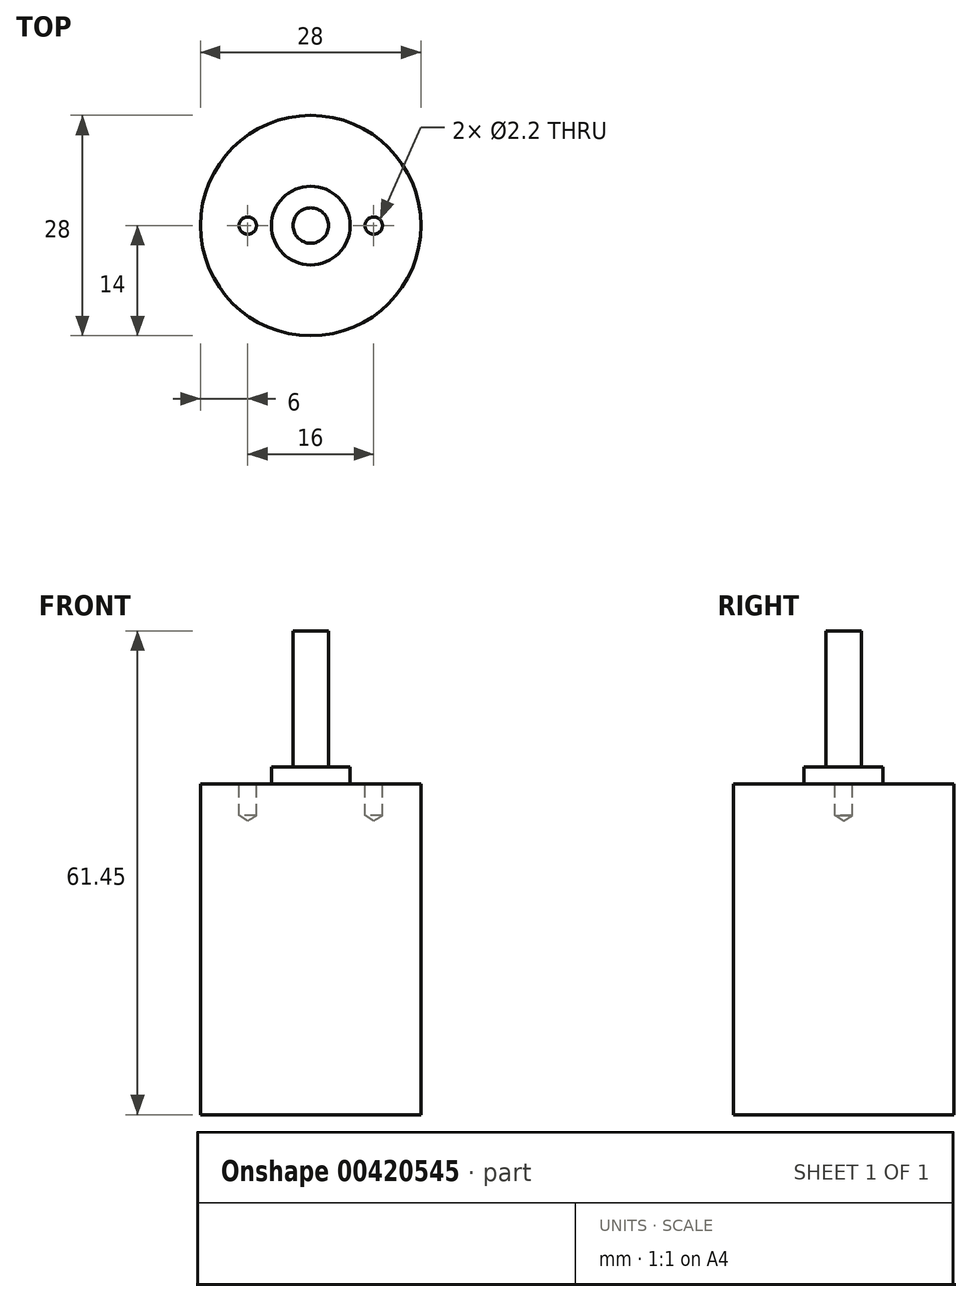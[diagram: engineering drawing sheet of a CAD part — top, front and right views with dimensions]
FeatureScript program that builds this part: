
annotation { "Feature Type Name" : "Feature", "Feature Type Description" : "" }
export const myFeature = defineFeature(function(context is Context, id is Id, definition is map)
    precondition{}
    {
        {
            var Q0;
            Q0=qCreatedBy(makeId("Top.planeOp"),FACE);
            var sketch = newSketch(context, id + "F0", { "sketchPlane" : qUnion([Q0])});
            skCircle(sketch, "E0", {"center": v(0, 0) * mm, "radius": 14 * mm});
            skSolve(sketch);
        }
        {
            var Q0;
            Q0=makeQuery(id+"F0.imprint","IMPRINT",FACE,{"disambiguationData":[TD([[makeQuery(id+"F0.imprint","IMPRINT",EDGE,{"derivedFrom":sQuery(id+"F0.wireOp",EDGE,"E0")}),1.0]])]});
            extrude(context, id + "F1", {"entities" : qUnion([Q0]), "depth" : 42 * mm});
        }
        {
            var Q0;
            Q0=makeQuery(id+"F1.opExtrude","CAP_FACE",FACE,{"disambiguationData":[OSD([sQuery(id+"F0.wireOp",EDGE,"E0")])],"isStart":false});
            var sketch = newSketch(context, id + "F2", { "sketchPlane" : qUnion([Q0])});
            skCircle(sketch, "E1", {"center": v(0, 0) * mm, "radius": 5 * mm});
            skPoint(sketch, "E2", {"position": v(-8, 0) * mm});
            skPoint(sketch, "E3", {"position": v(8, 0) * mm});
            skSolve(sketch);
        }
        {
            var Q0;
            Q0=makeQuery(id+"F2.imprint","IMPRINT",FACE,{"disambiguationData":[TD([[makeQuery(id+"F2.imprint","IMPRINT",EDGE,{"derivedFrom":sQuery(id+"F2.wireOp",EDGE,"E1")}),1.0]])]});
            extrude(context, id + "F3", {"entities" : qUnion([Q0]), "operationType" : NewBodyOperationType.ADD, "depth" : 2.2 * mm});
        }
        {
            var Q0;
            Q0=makeQuery(id+"F3.opExtrude","CAP_FACE",FACE,{"disambiguationData":[OSD([sQuery(id+"F2.wireOp",EDGE,"E1")])],"isStart":false});
            var sketch = newSketch(context, id + "F4", { "sketchPlane" : qUnion([Q0])});
            skCircle(sketch, "E4", {"center": v(0, 0) * mm, "radius": 2.25 * mm});
            skSolve(sketch);
        }
        {
            var Q0;
            Q0=makeQuery(id+"F4.imprint","IMPRINT",FACE,{"disambiguationData":[TD([[makeQuery(id+"F4.imprint","IMPRINT",EDGE,{"derivedFrom":sQuery(id+"F4.wireOp",EDGE,"E4")}),1.0]])]});
            extrude(context, id + "F5", {"entities" : qUnion([Q0]), "operationType" : NewBodyOperationType.ADD, "depth" : (22 - 4.75) * mm});
        }
        {
            var Q0;
            Q0=sQuery(id+"F2.wireOp",VERTEX,"E2");
            var Q1;
            Q1=sQuery(id+"F2.wireOp",VERTEX,"E3");
            var Q2;
            Q2=makeQuery(id+"F1.opExtrude","SWEPT_BODY",BODY,{"disambiguationData":[OSD([sQuery(id+"F0.wireOp",EDGE,"E0")])]});
            hole(context, id + "F6", {"style" : HoleStyle.SIMPLE, "endStyle" : HoleEndStyle.BLIND, "holeDiameter" : 2.2 * mm, "holeDepth" : 4 * mm, "isTappedThrough" : true, "tappedDepth" : 12 * mm, "tapClearance" : 3, "locations" : qUnion([Q0, Q1]), "scope" : qUnion([Q2])});
        }
    });
